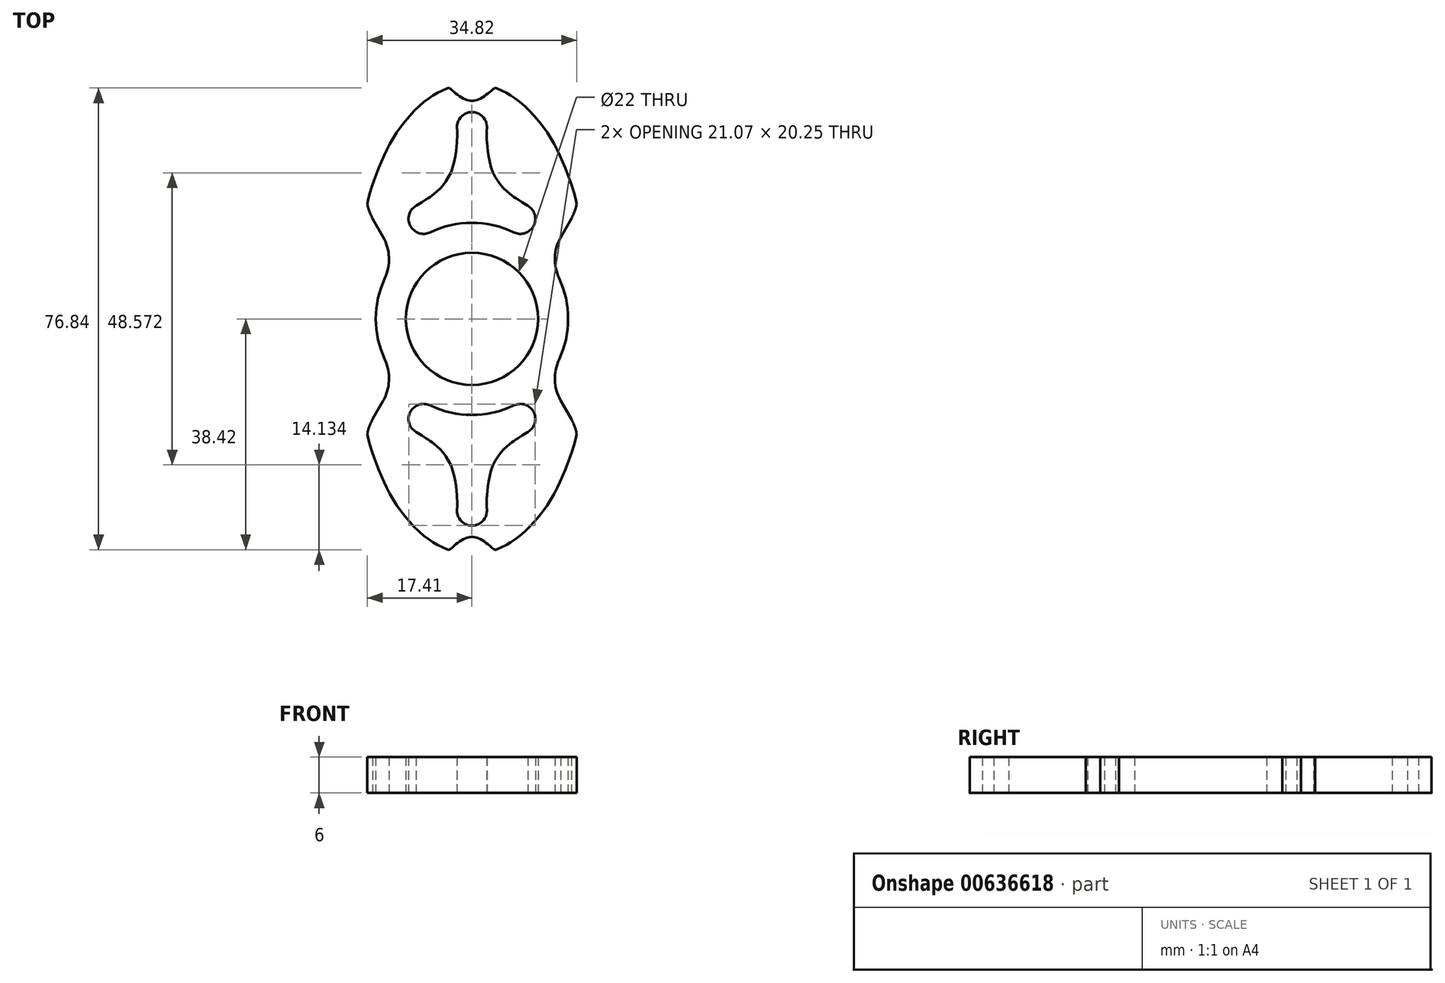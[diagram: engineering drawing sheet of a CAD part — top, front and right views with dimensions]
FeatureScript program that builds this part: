
annotation { "Feature Type Name" : "Feature", "Feature Type Description" : "" }
export const myFeature = defineFeature(function(context is Context, id is Id, definition is map)
    precondition{}
    {
        {
            var Q0;
            Q0=qCreatedBy(makeId("Top.planeOp"),FACE);
            var sketch = newSketch(context, id + "F0", { "sketchPlane" : qUnion([Q0])});
            skArc(sketch, "E0", {"start": v(16, 0) * mm, "mid": v(15.13, 5.21) * mm, "end": v(12.6, 9.86) * mm});
            skArc(sketch, "E1", {"start": v(11, 0) * mm, "mid": v(0, 11) * mm, "end": v(-11, 0) * mm});
            skLineSegment(sketch, "E2", {"start": v(0, 36.3) * mm, "end": v(0, 0) * mm, "construction": true});
            skFitSpline(sketch, "E3", {"points": [v(17.41, 16.19) * mm, v(17.41, 19.08) * mm, v(15.54, 25.05) * mm, v(12.52, 31.03) * mm, v(7.74, 36.3) * mm, v(3.84, 38.5) * mm], "startDerivative": vector(1.86, 12.58) * mm, "endDerivative": vector(-23.54, 9.7) * mm});
            skFitSpline(sketch, "E4.MirrorCS", {"points": [v(-17.41, 16.19) * mm, v(-17.41, 19.08) * mm, v(-15.54, 25.05) * mm, v(-12.52, 31.03) * mm, v(-7.74, 36.3) * mm, v(-3.84, 38.5) * mm], "startDerivative": vector(-1.86, 12.58) * mm, "endDerivative": vector(23.54, 9.7) * mm});
            skArc(sketch, "E5", {"start": v(2.5, 31.9) * mm, "mid": v(0, 34.4) * mm, "end": v(-2.5, 31.9) * mm});
            skArc(sketch, "E6", {"start": v(-9.3, 18.82) * mm, "mid": v(-10.26, 15.48) * mm, "end": v(-6.96, 14.4) * mm});
            skArc(sketch, "E7.MirrorC", {"start": v(9.3, 18.82) * mm, "mid": v(10.26, 15.48) * mm, "end": v(6.96, 14.4) * mm});
            skCircle(sketch, "E8", {"center": v(0, 21.92) * mm, "radius": 3 * mm, "construction": true});
            skFitSpline(sketch, "E9", {"points": [v(-2.5, 31.9) * mm, v(-2.49, 29.65) * mm, v(-3.62, 24.11) * mm, v(-6.5, 20.64) * mm, v(-9.3, 18.82) * mm], "startDerivative": vector(1.05, -19.69) * mm, "endDerivative": vector(-25.78, -16.42) * mm});
            skFitSpline(sketch, "E10.MirrorCS", {"points": [v(2.5, 31.9) * mm, v(2.49, 29.65) * mm, v(3.62, 24.11) * mm, v(6.5, 20.64) * mm, v(9.3, 18.82) * mm], "startDerivative": vector(-1.05, -19.69) * mm, "endDerivative": vector(25.78, -16.42) * mm});
            skArc(sketch, "E11.trimOffspring", {"start": v(6.96, 14.4) * mm, "mid": v(0, 16) * mm, "end": v(-6.96, 14.4) * mm});
            skArc(sketch, "E12.trimOffspring", {"start": v(-14.5, 6.76) * mm, "mid": v(-15.62, 3.46) * mm, "end": v(-16, 0) * mm});
            skLineSegment(sketch, "E13.trimOffspring", {"start": v(-14.76, 13.59) * mm, "end": v(-16.55, 16.69) * mm});
            skPoint(sketch, "E14.end.orphan", {"position": v(6.48, 0) * mm});
            skPoint(sketch, "E15.MirrorCS.start.orphan", {"position": v(-6.48, 0) * mm});
            skPoint(sketch, "E16.orphan", {"position": v(-7.05, 36.3) * mm});
            skPoint(sketch, "E17.end.orphan", {"position": v(7.05, 36.3) * mm});
            skArc(sketch, "E18.MirrorCS", {"start": v(-11, 0) * mm, "mid": v(0, 11) * mm, "end": v(11, 0) * mm});
            skArc(sketch, "E19.MirrorCS", {"start": v(-16, 0) * mm, "mid": v(-15.13, 5.21) * mm, "end": v(-12.6, 9.86) * mm});
            skArc(sketch, "E20.MirrorCS", {"start": v(-6.96, 14.4) * mm, "mid": v(0, 16) * mm, "end": v(6.96, 14.4) * mm});
            skArc(sketch, "E21.MirrorCS", {"start": v(-2.5, 31.9) * mm, "mid": v(0, 34.4) * mm, "end": v(2.5, 31.9) * mm});
            skArc(sketch, "E22.MirrorCS", {"start": v(12.6, 9.86) * mm, "mid": v(15.13, 5.21) * mm, "end": v(16, 0) * mm});
            skLineSegment(sketch, "E23.MirrorCS", {"start": v(-14.8, 13.67) * mm, "end": v(-16.55, 16.69) * mm});
            skArc(sketch, "E24.MirrorCS", {"start": v(-12.6, 9.86) * mm, "mid": v(-15.13, 5.21) * mm, "end": v(-16, 0) * mm});
            skFitSpline(sketch, "E25.MirrorCS", {"points": [v(2.5, 31.9) * mm, v(2.49, 29.65) * mm, v(3.62, 24.11) * mm, v(6.5, 20.64) * mm, v(9.3, 18.82) * mm], "startDerivative": vector(-1.05, -19.69) * mm, "endDerivative": vector(25.78, -16.42) * mm});
            skLineSegment(sketch, "E26.MirrorCS", {"start": v(-14.76, 13.59) * mm, "end": v(-15.93, 15.63) * mm});
            skFitSpline(sketch, "E27.MirrorCS", {"points": [v(17.41, 16.19) * mm, v(17.41, 19.08) * mm, v(15.54, 25.05) * mm, v(12.52, 31.03) * mm, v(7.74, 36.3) * mm, v(3.84, 38.5) * mm], "startDerivative": vector(1.86, 12.58) * mm, "endDerivative": vector(-23.54, 9.7) * mm});
            skLineSegment(sketch, "E28", {"start": v(-16, 0) * mm, "end": v(-11, 0) * mm});
            skLineSegment(sketch, "E29", {"start": v(11, 0) * mm, "end": v(16, 0) * mm});
            skLineSegment(sketch, "E30", {"start": v(-15.14, 9.86) * mm, "end": v(15.05, 9.86) * mm, "construction": true});
            skFitSpline(sketch, "E31", {"points": [v(16.55, 16.69) * mm, v(17.41, 19.08) * mm, v(17.41, 22.3) * mm], "startDerivative": vector(2.27, 4.84) * mm, "endDerivative": vector(-0.49, 6.34) * mm});
            skFitSpline(sketch, "E32.MirrorCS", {"points": [v(-16.55, 16.69) * mm, v(-17.41, 19.08) * mm, v(-17.41, 22.3) * mm], "startDerivative": vector(-2.27, 4.84) * mm, "endDerivative": vector(0.49, 6.34) * mm});
            skFitSpline(sketch, "E33", {"points": [v(-3.84, 38.5) * mm, v(0, 36.3) * mm, v(3.84, 38.5) * mm], "startDerivative": vector(7.68, -6.6) * mm, "endDerivative": vector(7.68, 6.6) * mm});
            skPoint(sketch, "E34.newPointA", {"position": v(-12.6, 9.86) * mm});
            skPoint(sketch, "E34.newPointB", {"position": v(-12.6, 9.86) * mm});
            skArc(sketch, "E34.filletArc", {"start": v(-14.5, 6.76) * mm, "mid": v(-13.8, 10.25) * mm, "end": v(-14.8, 13.67) * mm});
            skArc(sketch, "E35.MirrorCS", {"start": v(14.5, 6.76) * mm, "mid": v(13.8, 10.25) * mm, "end": v(14.8, 13.67) * mm});
            skLineSegment(sketch, "E36.MirrorCS", {"start": v(14.76, 13.59) * mm, "end": v(16.55, 16.69) * mm});
            skArc(sketch, "E37.filletArc", {"start": v(-3.6, 38.3) * mm, "mid": v(-3.85, 38.42) * mm, "end": v(-4.12, 38.38) * mm});
            skArc(sketch, "E38.filletArc", {"start": v(4.12, 38.38) * mm, "mid": v(3.85, 38.42) * mm, "end": v(3.6, 38.3) * mm});
            skSolve(sketch);
        }
        {
            var Q0;
            Q0=makeQuery(id+"F0.imprint","IMPRINT",FACE,{"disambiguationData":[TD([[makeQuery(id+"F0.imprint","IMPRINT",EDGE,{"derivedFrom":sQuery(id+"F0.wireOp",EDGE,"E9")}),-1.0]])]});
            var Q1;
            {var subQ0=sQuery(id+"F0.wireOp",EDGE,"E24.MirrorCS");var subQ3=sQuery(id+"F0.wireOp",EDGE,"E34.filletArc");var subQ5=makeQuery(id+"F0.imprint","INTERSECT",VERTEX,{"derivedFrom":[subQ0,subQ3]});Q1=makeQuery(id+"F0.imprint","IMPRINT",FACE,{"disambiguationData":[TD([[makeQuery(id+"F0.imprint","IMPRINT",EDGE,{"disambiguationData":[TD([[subQ5,-1.0]])],"derivedFrom":subQ3}),-1.0]])]});}
            var Q2;
            {var subQ0=sQuery(id+"F0.wireOp",EDGE,"E22.MirrorCS");var subQ3=sQuery(id+"F0.wireOp",EDGE,"E35.MirrorCS");var subQ5=makeQuery(id+"F0.imprint","INTERSECT",VERTEX,{"derivedFrom":[subQ0,subQ3]});Q2=makeQuery(id+"F0.imprint","IMPRINT",FACE,{"disambiguationData":[TD([[makeQuery(id+"F0.imprint","IMPRINT",EDGE,{"disambiguationData":[TD([[subQ5,-1.0]])],"derivedFrom":subQ3}),1.0]])]});}
            extrude(context, id + "F1", {"entities" : qUnion([Q0, Q1, Q2]), "depth" : 6 * mm, "offsetDistance" : 25 * mm});
        }
        {
            var Q0;
            Q0=makeQuery(id+"F1.opExtrude","SWEPT_BODY",BODY,{"disambiguationData":[OSD([sQuery(id+"F0.wireOp",EDGE,"31b44a5d-2370-4149-a95d-7eb2823e4dba.MirrorCS"),sQuery(id+"F0.wireOp",EDGE,"6bc757db-ac33-4326-bd76-50ec68fa99e9.MirrorCS"),sQuery(id+"F0.wireOp",EDGE,"d590bcbf-da63-4d7e-acac-e686088b15d5.MirrorCS"),sQuery(id+"F0.wireOp",EDGE,"fa08a352-39bd-4d10-a374-3d60ca1ece5b.MirrorCS"),sQuery(id+"F0.wireOp",EDGE,"57518ed6-8dd4-4740-a970-7f321be1fc66.MirrorCS"),sQuery(id+"F0.wireOp",EDGE,"74c9a5db-0392-44a4-a840-815879a16b2d.MirrorCS"),sQuery(id+"F0.wireOp",EDGE,"a0bfb35d-09b9-4d76-b3dd-5ff767338f59.MirrorCS"),sQuery(id+"F0.wireOp",EDGE,"9728a9c9-98c5-4b3d-aa98-23b63130cd2b.MirrorCS"),sQuery(id+"F0.wireOp",EDGE,"E9"),sQuery(id+"F0.wireOp",EDGE,"730ccd0e-3457-435c-96dd-dc8f95664126.MirrorCS"),sQuery(id+"F0.wireOp",EDGE,"E7.MirrorC"),sQuery(id+"F0.wireOp",EDGE,"c3cc56b2-5268-4a23-94d4-aa40b3622f2a.MirrorCS"),sQuery(id+"F0.wireOp",EDGE,"E3"),sQuery(id+"F0.wireOp",EDGE,"E6"),sQuery(id+"F0.wireOp",EDGE,"E5"),sQuery(id+"F0.wireOp",EDGE,"E19.MirrorCS"),sQuery(id+"F0.wireOp",EDGE,"E4.MirrorCS"),sQuery(id+"F0.wireOp",EDGE,"E0"),sQuery(id+"F0.wireOp",EDGE,"E22.MirrorCS"),sQuery(id+"F0.wireOp",EDGE,"E1"),sQuery(id+"F0.wireOp",EDGE,"E24.MirrorCS"),sQuery(id+"F0.wireOp",EDGE,"E25.MirrorCS"),sQuery(id+"F0.wireOp",EDGE,"E11.trimOffspring"),sQuery(id+"F0.wireOp",EDGE,"E28"),sQuery(id+"F0.wireOp",EDGE,"E29")])]});
            var Q1;
            Q1=qCreatedBy(makeId("Front.planeOp"),FACE);
            mirror(context, id + "F2", {"operationType" : NewBodyOperationType.ADD, "entities" : qUnion([Q0]), "mirrorPlane" : qUnion([Q1])});
        }
    });
